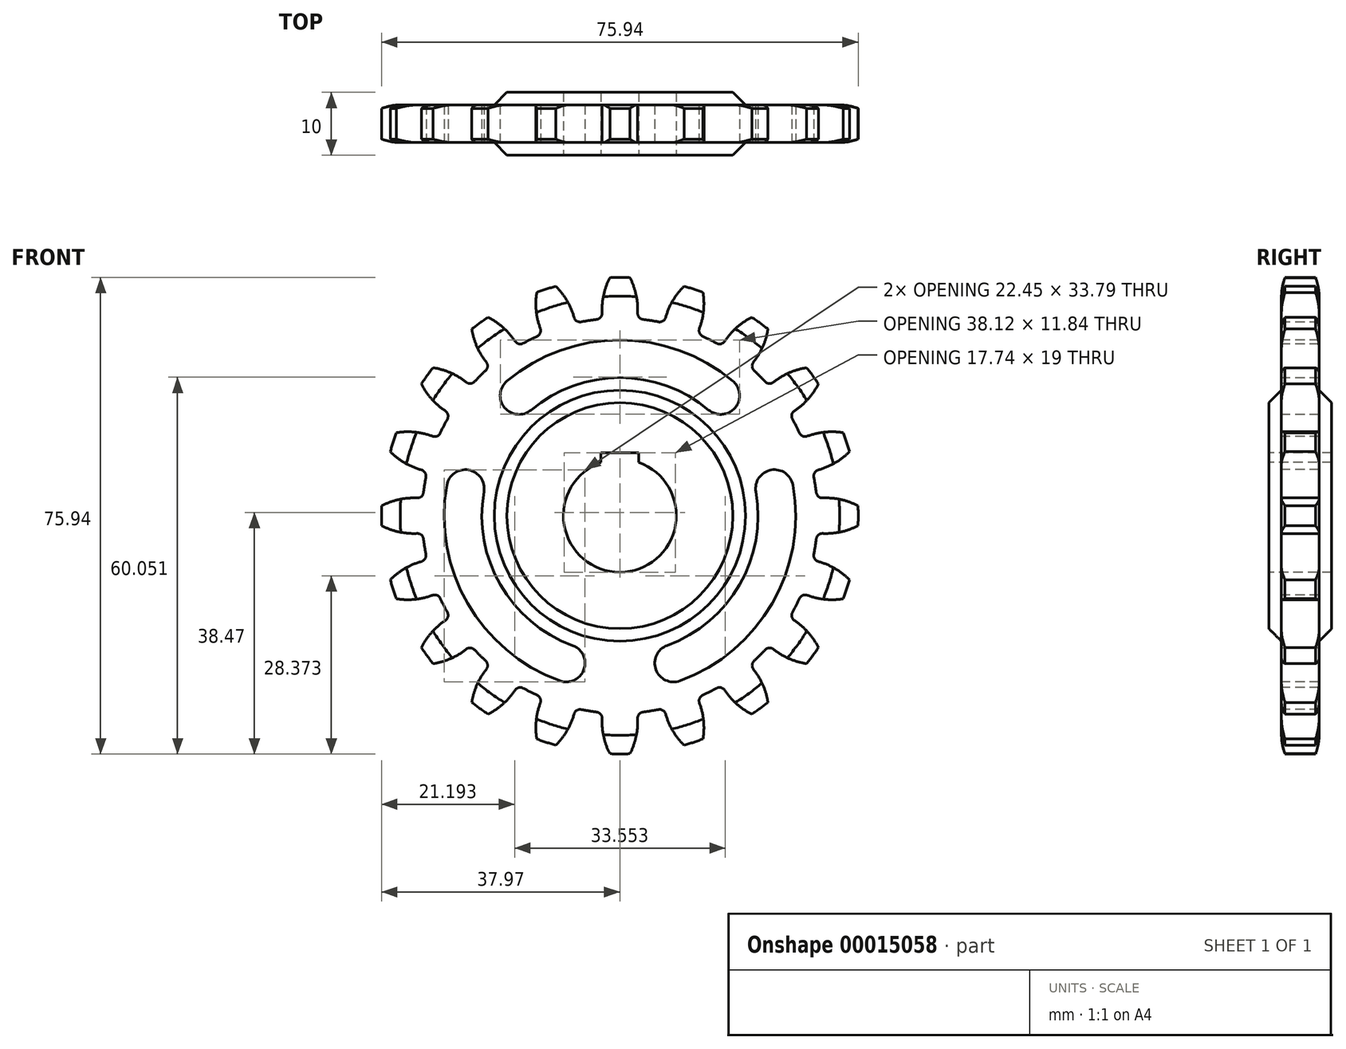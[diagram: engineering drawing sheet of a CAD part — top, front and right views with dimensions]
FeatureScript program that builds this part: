
annotation { "Feature Type Name" : "Feature", "Feature Type Description" : "" }
export const myFeature = defineFeature(function(context is Context, id is Id, definition is map)
    precondition{}
    {
        {
            var Q0;
            Q0=qCreatedBy(makeId("Front.planeOp"),FACE);
            var sketch = newSketch(context, id + "F0", { "sketchPlane" : qUnion([Q0])});
            skCircle(sketch, "E0", {"center": v(0, 0) * mm, "radius": 31.5 * mm});
            skCircle(sketch, "E1", {"center": v(0, 0) * mm, "radius": 38 * mm});
            skLineSegment(sketch, "E2", {"start": v(0, 0) * mm, "end": v(0, 38) * mm, "construction": true});
            skCircle(sketch, "E3", {"center": v(0, 0) * mm, "radius": 35 * mm, "construction": true});
            skLineSegment(sketch, "E4.rect.left", {"start": v(2.75, 31.38) * mm, "end": v(2.75, 34.9) * mm, "construction": true});
            skLineSegment(sketch, "E4.rect.right", {"start": v(-2.75, 31.38) * mm, "end": v(-2.75, 34.9) * mm, "construction": true});
            skPoint(sketch, "E4.rect.middle", {"position": v(0, 35) * mm});
            skLineSegment(sketch, "E5.rect.left", {"start": v(1.57, 34.96) * mm, "end": v(1.57, 37.97) * mm, "construction": true});
            skLineSegment(sketch, "E5.rect.right", {"start": v(-1.57, 34.96) * mm, "end": v(-1.57, 37.97) * mm, "construction": true});
            skPoint(sketch, "E6", {"position": v(0, 31.5) * mm});
            skPoint(sketch, "E7.orphan", {"position": v(2.75, 38.62) * mm});
            skPoint(sketch, "E8.orphan", {"position": v(-2.75, 38.62) * mm});
            skPoint(sketch, "E9.orphan", {"position": v(1.57, 32.03) * mm});
            skPoint(sketch, "E10.orphan", {"position": v(-1.57, 32.03) * mm});
            skPoint(sketch, "E11.orphan", {"position": v(2.75, 31.38) * mm});
            skPoint(sketch, "E4.rect.bottom.end.orphan", {"position": v(-2.75, 31.38) * mm});
            skArc(sketch, "E12", {"start": v(-1.57, 37.97) * mm, "mid": v(-2.67, 34.76) * mm, "end": v(-2.75, 31.38) * mm});
            skArc(sketch, "E13.0.MirrorCS", {"start": v(1.57, 37.97) * mm, "mid": v(2.67, 34.76) * mm, "end": v(2.75, 31.38) * mm});
            skSolve(sketch);
        }
        {
            var Q0;
            {var subQ0=sQuery(id+"F0.wireOp",EDGE,"E0");var subQ2=makeQuery(id+"F0.imprint","INTERSECT",VERTEX,{"derivedFrom":[subQ0,sQuery(id+"F0.wireOp",EDGE,"E12")]});Q0=makeQuery(id+"F0.imprint","IMPRINT",FACE,{"disambiguationData":[TD([[makeQuery(id+"F0.imprint","IMPRINT",EDGE,{"disambiguationData":[TD([[subQ2,1.0]])],"derivedFrom":subQ0}),1.0]])]});}
            var Q1;
            {var subQ1=sQuery(id+"F0.wireOp",EDGE,"E12");Q1=makeQuery(id+"F0.imprint","IMPRINT",FACE,{"disambiguationData":[TD([[makeQuery(id+"F0.imprint","IMPRINT",EDGE,{"derivedFrom":subQ1}),1.0]])]});}
            extrude(context, id + "F1", {"entities" : qUnion([Q0, Q1]), "endBound" : BoundingType.SYMMETRIC, "depth" : 10 * mm});
        }
        {
            var Q0;
            Q0=makeQuery(id+"F1.opExtrude","SWEPT_EDGE",EDGE,{"disambiguationData":[OSD([sQuery(id+"F0.wireOp",EDGE,"E0"),sQuery(id+"F0.wireOp",EDGE,"E12")])]});
            var Q1;
            Q1=makeQuery(id+"F1.opExtrude","SWEPT_EDGE",EDGE,{"disambiguationData":[OSD([sQuery(id+"F0.wireOp",EDGE,"E0"),sQuery(id+"F0.wireOp",EDGE,"E13.0.MirrorCS")])]});
            fillet(context, id + "F2", {"entities" : qUnion([Q0, Q1]), "radius" : 1 * mm, "tangentPropagation" : true, "allowEdgeOverflow" : false});
        }
        {
            var Q0;
            Q0=makeQuery(id+"F1.opExtrude","SWEPT_BODY",BODY,{"disambiguationData":[OSD([sQuery(id+"F0.wireOp",EDGE,"E0"),sQuery(id+"F0.wireOp",EDGE,"E1"),sQuery(id+"F0.wireOp",EDGE,"E12"),sQuery(id+"F0.wireOp",EDGE,"E13.0.MirrorCS")])]});
            var Q1;
            Q1=makeQuery(id+"F1.opExtrude","CAP_EDGE",EDGE,{"disambiguationData":[OSD([sQuery(id+"F0.wireOp",EDGE,"E0")])],"isStart":false});
            circularPattern(context, id + "F3", {"entities" : qUnion([Q0]), "axis" : qUnion([Q1]), "angle" : 360 * degree, "instanceCount" : round(20), "equalSpace" : true});
        }
        {
            var Q0;
            Q0=makeQuery(id+"F1.opExtrude","SWEPT_BODY",BODY,{"disambiguationData":[OSD([sQuery(id+"F0.wireOp",EDGE,"E0"),sQuery(id+"F0.wireOp",EDGE,"E1"),sQuery(id+"F0.wireOp",EDGE,"E12"),sQuery(id+"F0.wireOp",EDGE,"E13.0.MirrorCS")])]});
            var Q1;
            Q1=makeQuery(id+"F3.opPattern","COPY",BODY,{"derivedFrom":makeQuery(id+"F1.opExtrude","SWEPT_BODY",BODY,{"disambiguationData":[OSD([sQuery(id+"F0.wireOp",EDGE,"E0"),sQuery(id+"F0.wireOp",EDGE,"E1"),sQuery(id+"F0.wireOp",EDGE,"E12"),sQuery(id+"F0.wireOp",EDGE,"E13.0.MirrorCS")])]}),"instanceName":"1"});
            var Q2;
            Q2=makeQuery(id+"F3.opPattern","COPY",BODY,{"derivedFrom":makeQuery(id+"F1.opExtrude","SWEPT_BODY",BODY,{"disambiguationData":[OSD([sQuery(id+"F0.wireOp",EDGE,"E0"),sQuery(id+"F0.wireOp",EDGE,"E1"),sQuery(id+"F0.wireOp",EDGE,"E12"),sQuery(id+"F0.wireOp",EDGE,"E13.0.MirrorCS")])]}),"instanceName":"2"});
            var Q3;
            Q3=makeQuery(id+"F3.opPattern","COPY",BODY,{"derivedFrom":makeQuery(id+"F1.opExtrude","SWEPT_BODY",BODY,{"disambiguationData":[OSD([sQuery(id+"F0.wireOp",EDGE,"E0"),sQuery(id+"F0.wireOp",EDGE,"E1"),sQuery(id+"F0.wireOp",EDGE,"E12"),sQuery(id+"F0.wireOp",EDGE,"E13.0.MirrorCS")])]}),"instanceName":"3"});
            var Q4;
            Q4=makeQuery(id+"F3.opPattern","COPY",BODY,{"derivedFrom":makeQuery(id+"F1.opExtrude","SWEPT_BODY",BODY,{"disambiguationData":[OSD([sQuery(id+"F0.wireOp",EDGE,"E0"),sQuery(id+"F0.wireOp",EDGE,"E1"),sQuery(id+"F0.wireOp",EDGE,"E12"),sQuery(id+"F0.wireOp",EDGE,"E13.0.MirrorCS")])]}),"instanceName":"4"});
            var Q5;
            Q5=makeQuery(id+"F3.opPattern","COPY",BODY,{"derivedFrom":makeQuery(id+"F1.opExtrude","SWEPT_BODY",BODY,{"disambiguationData":[OSD([sQuery(id+"F0.wireOp",EDGE,"E0"),sQuery(id+"F0.wireOp",EDGE,"E1"),sQuery(id+"F0.wireOp",EDGE,"E12"),sQuery(id+"F0.wireOp",EDGE,"E13.0.MirrorCS")])]}),"instanceName":"5"});
            var Q6;
            Q6=makeQuery(id+"F3.opPattern","COPY",BODY,{"derivedFrom":makeQuery(id+"F1.opExtrude","SWEPT_BODY",BODY,{"disambiguationData":[OSD([sQuery(id+"F0.wireOp",EDGE,"E0"),sQuery(id+"F0.wireOp",EDGE,"E1"),sQuery(id+"F0.wireOp",EDGE,"E12"),sQuery(id+"F0.wireOp",EDGE,"E13.0.MirrorCS")])]}),"instanceName":"6"});
            var Q7;
            Q7=makeQuery(id+"F3.opPattern","COPY",BODY,{"derivedFrom":makeQuery(id+"F1.opExtrude","SWEPT_BODY",BODY,{"disambiguationData":[OSD([sQuery(id+"F0.wireOp",EDGE,"E0"),sQuery(id+"F0.wireOp",EDGE,"E1"),sQuery(id+"F0.wireOp",EDGE,"E12"),sQuery(id+"F0.wireOp",EDGE,"E13.0.MirrorCS")])]}),"instanceName":"7"});
            var Q8;
            Q8=makeQuery(id+"F3.opPattern","COPY",BODY,{"derivedFrom":makeQuery(id+"F1.opExtrude","SWEPT_BODY",BODY,{"disambiguationData":[OSD([sQuery(id+"F0.wireOp",EDGE,"E0"),sQuery(id+"F0.wireOp",EDGE,"E1"),sQuery(id+"F0.wireOp",EDGE,"E12"),sQuery(id+"F0.wireOp",EDGE,"E13.0.MirrorCS")])]}),"instanceName":"8"});
            var Q9;
            Q9=makeQuery(id+"F3.opPattern","COPY",BODY,{"derivedFrom":makeQuery(id+"F1.opExtrude","SWEPT_BODY",BODY,{"disambiguationData":[OSD([sQuery(id+"F0.wireOp",EDGE,"E0"),sQuery(id+"F0.wireOp",EDGE,"E1"),sQuery(id+"F0.wireOp",EDGE,"E12"),sQuery(id+"F0.wireOp",EDGE,"E13.0.MirrorCS")])]}),"instanceName":"9"});
            var Q10;
            Q10=makeQuery(id+"F3.opPattern","COPY",BODY,{"derivedFrom":makeQuery(id+"F1.opExtrude","SWEPT_BODY",BODY,{"disambiguationData":[OSD([sQuery(id+"F0.wireOp",EDGE,"E0"),sQuery(id+"F0.wireOp",EDGE,"E1"),sQuery(id+"F0.wireOp",EDGE,"E12"),sQuery(id+"F0.wireOp",EDGE,"E13.0.MirrorCS")])]}),"instanceName":"10"});
            var Q11;
            Q11=makeQuery(id+"F3.opPattern","COPY",BODY,{"derivedFrom":makeQuery(id+"F1.opExtrude","SWEPT_BODY",BODY,{"disambiguationData":[OSD([sQuery(id+"F0.wireOp",EDGE,"E0"),sQuery(id+"F0.wireOp",EDGE,"E1"),sQuery(id+"F0.wireOp",EDGE,"E12"),sQuery(id+"F0.wireOp",EDGE,"E13.0.MirrorCS")])]}),"instanceName":"11"});
            var Q12;
            Q12=makeQuery(id+"F3.opPattern","COPY",BODY,{"derivedFrom":makeQuery(id+"F1.opExtrude","SWEPT_BODY",BODY,{"disambiguationData":[OSD([sQuery(id+"F0.wireOp",EDGE,"E0"),sQuery(id+"F0.wireOp",EDGE,"E1"),sQuery(id+"F0.wireOp",EDGE,"E12"),sQuery(id+"F0.wireOp",EDGE,"E13.0.MirrorCS")])]}),"instanceName":"12"});
            var Q13;
            Q13=makeQuery(id+"F3.opPattern","COPY",BODY,{"derivedFrom":makeQuery(id+"F1.opExtrude","SWEPT_BODY",BODY,{"disambiguationData":[OSD([sQuery(id+"F0.wireOp",EDGE,"E0"),sQuery(id+"F0.wireOp",EDGE,"E1"),sQuery(id+"F0.wireOp",EDGE,"E12"),sQuery(id+"F0.wireOp",EDGE,"E13.0.MirrorCS")])]}),"instanceName":"13"});
            var Q14;
            Q14=makeQuery(id+"F3.opPattern","COPY",BODY,{"derivedFrom":makeQuery(id+"F1.opExtrude","SWEPT_BODY",BODY,{"disambiguationData":[OSD([sQuery(id+"F0.wireOp",EDGE,"E0"),sQuery(id+"F0.wireOp",EDGE,"E1"),sQuery(id+"F0.wireOp",EDGE,"E12"),sQuery(id+"F0.wireOp",EDGE,"E13.0.MirrorCS")])]}),"instanceName":"14"});
            var Q15;
            Q15=makeQuery(id+"F3.opPattern","COPY",BODY,{"derivedFrom":makeQuery(id+"F1.opExtrude","SWEPT_BODY",BODY,{"disambiguationData":[OSD([sQuery(id+"F0.wireOp",EDGE,"E0"),sQuery(id+"F0.wireOp",EDGE,"E1"),sQuery(id+"F0.wireOp",EDGE,"E12"),sQuery(id+"F0.wireOp",EDGE,"E13.0.MirrorCS")])]}),"instanceName":"15"});
            var Q16;
            Q16=makeQuery(id+"F3.opPattern","COPY",BODY,{"derivedFrom":makeQuery(id+"F1.opExtrude","SWEPT_BODY",BODY,{"disambiguationData":[OSD([sQuery(id+"F0.wireOp",EDGE,"E0"),sQuery(id+"F0.wireOp",EDGE,"E1"),sQuery(id+"F0.wireOp",EDGE,"E12"),sQuery(id+"F0.wireOp",EDGE,"E13.0.MirrorCS")])]}),"instanceName":"16"});
            var Q17;
            Q17=makeQuery(id+"F3.opPattern","COPY",BODY,{"derivedFrom":makeQuery(id+"F1.opExtrude","SWEPT_BODY",BODY,{"disambiguationData":[OSD([sQuery(id+"F0.wireOp",EDGE,"E0"),sQuery(id+"F0.wireOp",EDGE,"E1"),sQuery(id+"F0.wireOp",EDGE,"E12"),sQuery(id+"F0.wireOp",EDGE,"E13.0.MirrorCS")])]}),"instanceName":"17"});
            var Q18;
            Q18=makeQuery(id+"F3.opPattern","COPY",BODY,{"derivedFrom":makeQuery(id+"F1.opExtrude","SWEPT_BODY",BODY,{"disambiguationData":[OSD([sQuery(id+"F0.wireOp",EDGE,"E0"),sQuery(id+"F0.wireOp",EDGE,"E1"),sQuery(id+"F0.wireOp",EDGE,"E12"),sQuery(id+"F0.wireOp",EDGE,"E13.0.MirrorCS")])]}),"instanceName":"18"});
            var Q19;
            Q19=makeQuery(id+"F3.opPattern","COPY",BODY,{"derivedFrom":makeQuery(id+"F1.opExtrude","SWEPT_BODY",BODY,{"disambiguationData":[OSD([sQuery(id+"F0.wireOp",EDGE,"E0"),sQuery(id+"F0.wireOp",EDGE,"E1"),sQuery(id+"F0.wireOp",EDGE,"E12"),sQuery(id+"F0.wireOp",EDGE,"E13.0.MirrorCS")])]}),"instanceName":"19"});
            booleanBodies(context, id + "F4", {"operationType" : BooleanOperationType.UNION, "tools" : qUnion([Q0, Q1, Q2, Q3, Q4, Q5, Q6, Q7, Q8, Q9, Q10, Q11, Q12, Q13, Q14, Q15, Q16, Q17, Q18, Q19])});
        }
        {
            var Q0;
            {var subQ0=makeQuery(id+"F1.opExtrude","CAP_FACE",FACE,{"disambiguationData":[OSD([sQuery(id+"F0.wireOp",EDGE,"E0"),sQuery(id+"F0.wireOp",EDGE,"E1"),sQuery(id+"F0.wireOp",EDGE,"E12"),sQuery(id+"F0.wireOp",EDGE,"E13.0.MirrorCS")])],"isStart":false});Q0=makeQuery(id+"F4.opBoolean","MERGE",FACE,{"derivedFrom":[subQ0,makeQuery(id+"F3.opPattern","COPY",FACE,{"derivedFrom":subQ0,"instanceName":"1"}),makeQuery(id+"F3.opPattern","COPY",FACE,{"derivedFrom":subQ0,"instanceName":"2"}),makeQuery(id+"F3.opPattern","COPY",FACE,{"derivedFrom":subQ0,"instanceName":"3"}),makeQuery(id+"F3.opPattern","COPY",FACE,{"derivedFrom":subQ0,"instanceName":"4"}),makeQuery(id+"F3.opPattern","COPY",FACE,{"derivedFrom":subQ0,"instanceName":"5"}),makeQuery(id+"F3.opPattern","COPY",FACE,{"derivedFrom":subQ0,"instanceName":"6"}),makeQuery(id+"F3.opPattern","COPY",FACE,{"derivedFrom":subQ0,"instanceName":"7"}),makeQuery(id+"F3.opPattern","COPY",FACE,{"derivedFrom":subQ0,"instanceName":"8"}),makeQuery(id+"F3.opPattern","COPY",FACE,{"derivedFrom":subQ0,"instanceName":"9"}),makeQuery(id+"F3.opPattern","COPY",FACE,{"derivedFrom":subQ0,"instanceName":"10"}),makeQuery(id+"F3.opPattern","COPY",FACE,{"derivedFrom":subQ0,"instanceName":"11"}),makeQuery(id+"F3.opPattern","COPY",FACE,{"derivedFrom":subQ0,"instanceName":"12"}),makeQuery(id+"F3.opPattern","COPY",FACE,{"derivedFrom":subQ0,"instanceName":"13"}),makeQuery(id+"F3.opPattern","COPY",FACE,{"derivedFrom":subQ0,"instanceName":"14"}),makeQuery(id+"F3.opPattern","COPY",FACE,{"derivedFrom":subQ0,"instanceName":"15"}),makeQuery(id+"F3.opPattern","COPY",FACE,{"derivedFrom":subQ0,"instanceName":"16"}),makeQuery(id+"F3.opPattern","COPY",FACE,{"derivedFrom":subQ0,"instanceName":"17"}),makeQuery(id+"F3.opPattern","COPY",FACE,{"derivedFrom":subQ0,"instanceName":"18"}),makeQuery(id+"F3.opPattern","COPY",FACE,{"derivedFrom":subQ0,"instanceName":"19"})]});}
            var sketch = newSketch(context, id + "F5", { "sketchPlane" : qUnion([Q0])});
            skArc(sketch, "E14", {"start": v(-3, 8.49) * mm, "mid": v(0, -9) * mm, "end": v(3, 8.49) * mm});
            skLineSegment(sketch, "E15", {"start": v(0, 0) * mm, "end": v(0, 58.58) * mm, "construction": true});
            skLineSegment(sketch, "E16.rect.top", {"start": v(3, 10) * mm, "end": v(-3, 10) * mm});
            skLineSegment(sketch, "E16.rect.left", {"start": v(3, 8.49) * mm, "end": v(3, 10) * mm});
            skLineSegment(sketch, "E16.rect.right", {"start": v(-3, 8.49) * mm, "end": v(-3, 10) * mm});
            skPoint(sketch, "E16.rect.middle", {"position": v(0, 9) * mm});
            skPoint(sketch, "E17.orphan", {"position": v(-3, 8) * mm});
            skPoint(sketch, "E18.orphan", {"position": v(3, 8) * mm});
            skArc(sketch, "E19", {"start": v(18.25, 17.09) * mm, "mid": v(0, 25) * mm, "end": v(-18.25, 17.09) * mm, "construction": true});
            skArc(sketch, "E20", {"start": v(14.14, 16.85) * mm, "mid": v(0, 22) * mm, "end": v(-14.14, 16.85) * mm});
            skArc(sketch, "E21", {"start": v(18, 21.45) * mm, "mid": v(0, 28) * mm, "end": v(-18, 21.45) * mm});
            skLineSegment(sketch, "E22", {"start": v(0, 0) * mm, "end": v(31.58, 37.64) * mm, "construction": true});
            skLineSegment(sketch, "E23", {"start": v(-30.96, 36.9) * mm, "end": v(0, 0) * mm, "construction": true});
            skArc(sketch, "E24", {"start": v(-18, 21.45) * mm, "mid": v(-18.37, 17.22) * mm, "end": v(-14.14, 16.85) * mm});
            skArc(sketch, "E25", {"start": v(14.14, 16.85) * mm, "mid": v(18.37, 17.22) * mm, "end": v(18, 21.45) * mm});
            skArc(sketch, "E26.1.0", {"start": v(-27.57, 4.86) * mm, "mid": v(-24.25, -14) * mm, "end": v(-9.58, -26.31) * mm});
            skArc(sketch, "E26.1.1", {"start": v(-9.58, -26.31) * mm, "mid": v(-5.73, -24.52) * mm, "end": v(-7.52, -20.67) * mm});
            skArc(sketch, "E26.1.2", {"start": v(-21.67, 3.82) * mm, "mid": v(-19.05, -11) * mm, "end": v(-7.52, -20.67) * mm});
            skArc(sketch, "E26.1.3", {"start": v(-21.67, 3.82) * mm, "mid": v(-24.1, 7.3) * mm, "end": v(-27.57, 4.86) * mm});
            skArc(sketch, "E26.2.0", {"start": v(9.58, -26.31) * mm, "mid": v(24.25, -14) * mm, "end": v(27.57, 4.86) * mm});
            skArc(sketch, "E26.2.1", {"start": v(27.57, 4.86) * mm, "mid": v(24.1, 7.3) * mm, "end": v(21.67, 3.82) * mm});
            skArc(sketch, "E26.2.2", {"start": v(7.52, -20.67) * mm, "mid": v(19.05, -11) * mm, "end": v(21.67, 3.82) * mm});
            skArc(sketch, "E26.2.3", {"start": v(7.52, -20.67) * mm, "mid": v(5.73, -24.52) * mm, "end": v(9.58, -26.31) * mm});
            skSolve(sketch);
        }
        {
            var Q0;
            Q0=makeQuery(id+"F5.imprint","IMPRINT",FACE,{"disambiguationData":[TD([[makeQuery(id+"F5.imprint","IMPRINT",EDGE,{"derivedFrom":sQuery(id+"F5.wireOp",EDGE,"E14")}),1.0]])]});
            var Q1;
            Q1=makeQuery(id+"F5.imprint","IMPRINT",FACE,{"disambiguationData":[TD([[makeQuery(id+"F5.imprint","IMPRINT",EDGE,{"derivedFrom":sQuery(id+"F5.wireOp",EDGE,"E20")}),-1.0]])]});
            var Q2;
            Q2=makeQuery(id+"F5.imprint","IMPRINT",FACE,{"disambiguationData":[TD([[makeQuery(id+"F5.imprint","IMPRINT",EDGE,{"derivedFrom":sQuery(id+"F5.wireOp",EDGE,"E26.1.0")}),1.0]])]});
            var Q3;
            Q3=makeQuery(id+"F5.imprint","IMPRINT",FACE,{"disambiguationData":[TD([[makeQuery(id+"F5.imprint","IMPRINT",EDGE,{"derivedFrom":sQuery(id+"F5.wireOp",EDGE,"E26.2.0")}),1.0]])]});
            extrude(context, id + "F6", {"entities" : qUnion([Q0, Q1, Q2, Q3]), "operationType" : NewBodyOperationType.REMOVE, "endBound" : BoundingType.THROUGH_ALL, "oppositeDirection" : true, "depth" : 25 * mm});
        }
        {
            var Q0;
            Q0=qCreatedBy(makeId("Right.planeOp"),FACE);
            var sketch = newSketch(context, id + "F7", { "sketchPlane" : qUnion([Q0])});
            skLineSegment(sketch, "E27", {"start": v(0, 0) * mm, "end": v(0, 59.07) * mm});
            skLineSegment(sketch, "E28", {"start": v(0, 0) * mm, "end": v(15.65, 0) * mm});
            skLineSegment(sketch, "E29", {"start": v(5, 0) * mm, "end": v(5, 18) * mm});
            skLineSegment(sketch, "E30", {"start": v(5, 18) * mm, "end": v(3, 20) * mm});
            skLineSegment(sketch, "E31", {"start": v(3, 20) * mm, "end": v(3, 35) * mm});
            skLineSegment(sketch, "E32", {"start": v(2.43, 37.97) * mm, "end": v(0, 37.97) * mm});
            skLineSegment(sketch, "E33", {"start": v(0, 37.97) * mm, "end": v(0, 0) * mm});
            skLineSegment(sketch, "E34.0", {"start": v(-5, 37.97) * mm, "end": v(5, 37.97) * mm});
            skLineSegment(sketch, "E35.0.MirrorCS", {"start": v(-2.43, 37.97) * mm, "end": v(0, 37.97) * mm});
            skLineSegment(sketch, "E36.0.MirrorCS", {"start": v(-3, 20) * mm, "end": v(-3, 35) * mm});
            skLineSegment(sketch, "E37.0.MirrorCS", {"start": v(-5, 18) * mm, "end": v(-3, 20) * mm});
            skLineSegment(sketch, "E38.0.MirrorCS", {"start": v(-5, 0) * mm, "end": v(-5, 18) * mm});
            skLineSegment(sketch, "E39.0.MirrorCS", {"start": v(0, 0) * mm, "end": v(-15.65, 0) * mm});
            skArc(sketch, "E40", {"start": v(3, 35) * mm, "mid": v(2.85, 36.5) * mm, "end": v(2.43, 37.97) * mm});
            skArc(sketch, "E41.0.MirrorCS", {"start": v(-3, 35) * mm, "mid": v(-2.85, 36.5) * mm, "end": v(-2.43, 37.97) * mm});
            skLineSegment(sketch, "E42.top", {"start": v(-5, 0) * mm, "end": v(5, 0) * mm});
            skLineSegment(sketch, "E42.left", {"start": v(-5, 37.97) * mm, "end": v(-5, 0) * mm});
            skLineSegment(sketch, "E42.right", {"start": v(5, 37.97) * mm, "end": v(5, 0) * mm});
            skLineSegment(sketch, "E43", {"start": v(-5, 37.97) * mm, "end": v(-5, 40.05) * mm});
            skLineSegment(sketch, "E44", {"start": v(-5, 40.05) * mm, "end": v(5, 40.05) * mm});
            skLineSegment(sketch, "E45", {"start": v(5, 40.05) * mm, "end": v(5, 37.97) * mm});
            skSolve(sketch);
        }
        {
            var Q0;
            {var subQ3=sQuery(id+"F7.wireOp",EDGE,"E30");Q0=makeQuery(id+"F7.imprint","IMPRINT",FACE,{"disambiguationData":[TD([[makeQuery(id+"F7.imprint","IMPRINT",EDGE,{"derivedFrom":subQ3}),-1.0]])]});}
            var Q1;
            Q1=makeQuery(id+"F7.imprint","IMPRINT",FACE,{"disambiguationData":[TD([[makeQuery(id+"F7.imprint","IMPRINT",EDGE,{"derivedFrom":sQuery(id+"F7.wireOp",EDGE,"E36.0.MirrorCS")}),1.0]])]});
            var Q2;
            {var subQ3=sQuery(id+"F7.wireOp",EDGE,"E43");Q2=makeQuery(id+"F7.imprint","IMPRINT",FACE,{"disambiguationData":[TD([[makeQuery(id+"F7.imprint","IMPRINT",EDGE,{"derivedFrom":subQ3}),-1.0]])]});}
            var Q3;
            {var subQ3=sQuery(id+"F7.wireOp",EDGE,"E45");Q3=makeQuery(id+"F7.imprint","IMPRINT",FACE,{"disambiguationData":[TD([[makeQuery(id+"F7.imprint","IMPRINT",EDGE,{"derivedFrom":subQ3}),-1.0]])]});}
            var Q4;
            Q4=sQuery(id+"F7.wireOp",EDGE,"E39.0.MirrorCS");
            revolve(context, id + "F8", {"operationType" : NewBodyOperationType.REMOVE, "entities" : qUnion([Q0, Q1, Q2, Q3]), "axis" : qUnion([Q4]), "revolveType" : RevolveType.FULL, "oppositeDirection" : true});
        }
    });
